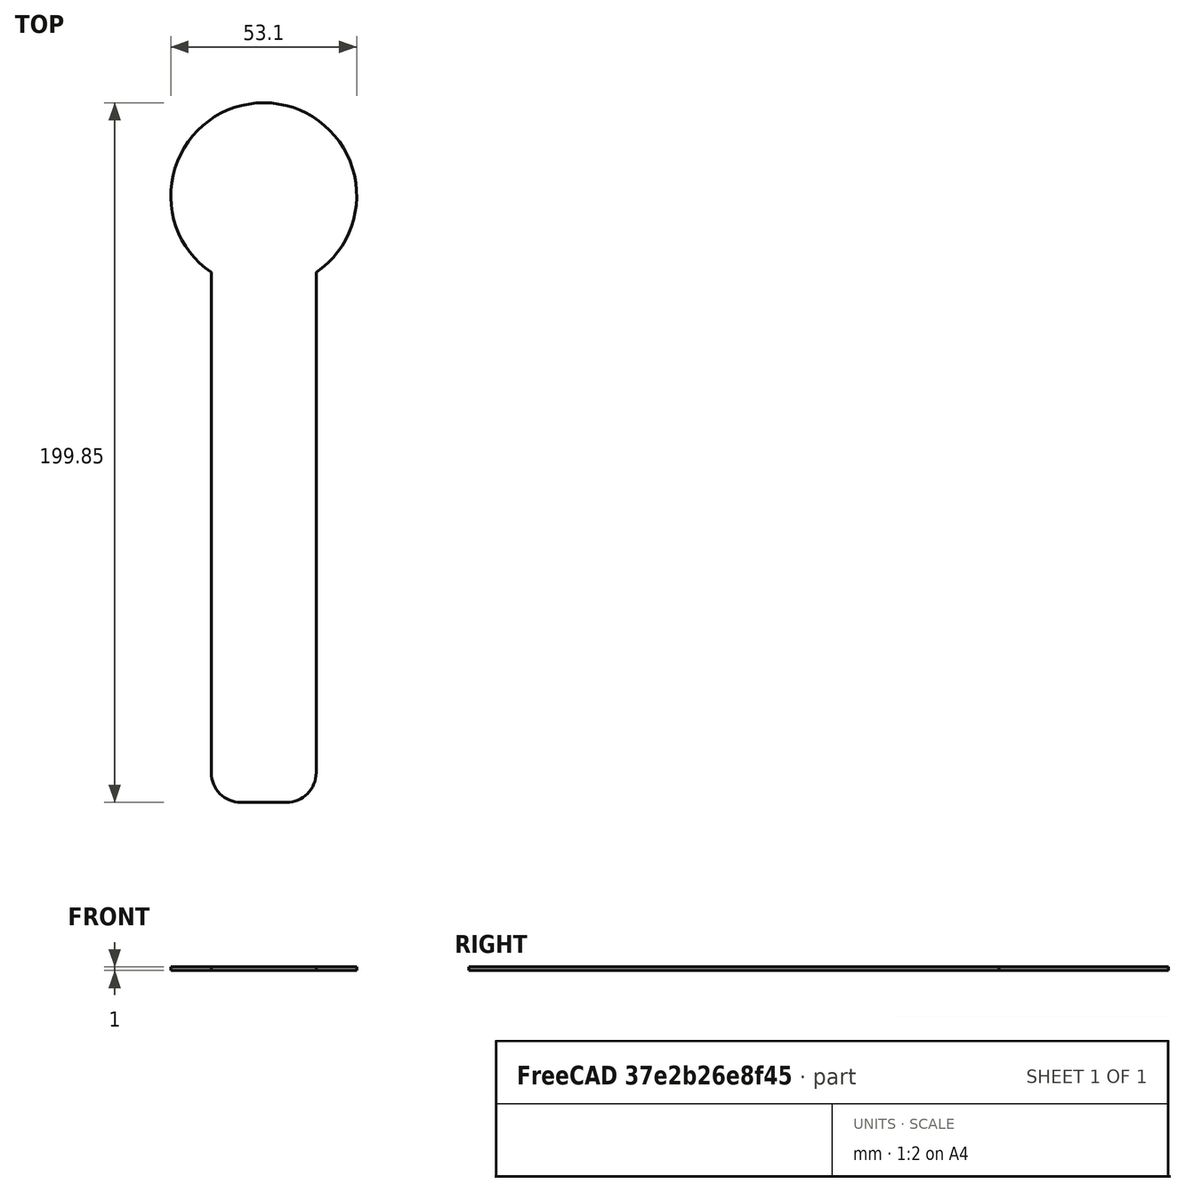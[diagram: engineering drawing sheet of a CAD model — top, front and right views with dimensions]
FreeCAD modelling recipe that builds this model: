
FCSTD DOCUMENT  (FreeCAD 1.0R39109 (Git))
Label: LinternaMonita
License: All rights reserved
LicenseURL: http://en.wikipedia.org/wiki/All_rights_reserved
objects: Sketcher::SketchObject×1, PartDesign::Pad×1, PartDesign::Body×1
note: 6 computed .brp shape members not serialized (recipe doc carries the construction recipe); baked Part::Feature solids carry a one-line shape summary decoded from their .brp

FEATURE [Sketcher::SketchObject] Sketch
  ArcFitTolerance = 1e-06
  AttachmentSupport = -> [XY_Plane]
  FullyConstrained = false
  MakeInternals = false
  MapMode = 5
  sketch-geometry (8):
    g0: LineSegment StartX=8.54141 StartY=0 StartZ=0 EndX=21.4586 EndY=0 EndZ=0
    g1: LineSegment StartX=30 StartY=8.54141 StartZ=0 EndX=30 EndY=151.391 EndZ=0
    g2: LineSegment StartX=0 StartY=151.391 StartZ=0 EndX=0 EndY=8.54141 EndZ=0
    g3: ArcOfCircle CenterX=15 CenterY=173.298 CenterZ=0 NormalX=0 NormalY=0 NormalZ=1 AngleXU=0 Radius=26.55 StartAngle=5.31279 EndAngle=10.3952
    g4: ArcOfCircle CenterX=8.54141 CenterY=8.54141 CenterZ=0 NormalX=0 NormalY=0 NormalZ=1 AngleXU=0 Radius=8.54141 StartAngle=3.14159 EndAngle=4.71239
    g5: GeomPoint [constr] X=0 Y=0 Z=0
    g6: ArcOfCircle CenterX=21.4586 CenterY=8.54141 CenterZ=0 NormalX=0 NormalY=0 NormalZ=1 AngleXU=0 Radius=8.54141 StartAngle=4.71239 EndAngle=6.28319
    g7: GeomPoint [constr] X=30 Y=0 Z=0
  constraints (18):
    c: Horizontal(g0)
    c: Vertical(g1)
    c: Vertical(g2)
    c: Distance(g7,g5) = 30
    c: Coincident(g5,g-1)
    c: Coincident(g3,g2)
    c: Coincident(g3,g1)
    c: PointOnObject(g5,g2)
    c: PointOnObject(g5,g0)
    c: Tangent(g2,g4) = -1.5708
    c: Tangent(g0,g4) = -1.5708
    c: PointOnObject(g7,g1)
    c: PointOnObject(g7,g0)
    c: Tangent(g1,g6) = -1.5708
    c: Tangent(g0,g6) = -1.5708
    c: Equal(g4,g6)
    c: Radius(g3) = 26.55
    c: Horizontal(g2,g1)
FEATURE [PartDesign::Pad] Pad
  Direction = (0,0,1)
  Length = 1
  Length2 = 10
  Profile = -> Sketch
  ReferenceAxis = -> Sketch [N_Axis]
  Suppressed = false
  Type = 0
FEATURE [PartDesign::Body] Body
  AllowCompound = false
  Group = -> [Sketch,Pad]
  Origin = -> Origin
  Tip = -> Pad
